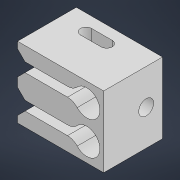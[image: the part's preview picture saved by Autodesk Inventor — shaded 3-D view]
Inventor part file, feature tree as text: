
AUTODESK INVENTOR PART (.ipt)
format: ipt  version: 2022 (Build 260153000, 153)  size: 280,064 bytes
history: native  units: in
note: dims shown in document units (in); Inventor stores cm internally (conversion verified against a paired STEP export)
features: sketch x14, extrude x8, plane x3, projected_geometry x3, chamfer x2, mirror x1
ambient origin geometry x8: Origin, YZ Plane, XZ Plane, XY Plane, X Axis, Y Axis, Z Axis, Center Point
bodies: Solid5 (feature_tree)
feature tree (31):
  plane  "Work Plane1"
  plane  "Work Plane2"
  sketch  "Sketch12"  dims[d45=0.3937in d46=0.0in d47=0.3937in d48=0.0in]
  extrude  "Extrusion15"  Depth=0.6693in TaperAngle=0.0deg
  extrude  "Extrusion16"  Depth=0.0984in TaperAngle=0.0deg
  chamfer  "Chamfer1"  Distance=0.2756in
  chamfer  "Chamfer2"  Distance=0.3937in
  extrude  "Extrusion18"  Depth=0.0787in
  plane  "Work Plane3"
  extrude  "Extrusion19"  Depth=0.1378in
  mirror  "Mirror1"
  extrude  "Extrusion20"  Depth=0.9055in
  extrude  "Extrusion22"  Depth=0.3937in TaperAngle=0.0deg
  extrude  "Extrusion23"  Depth=0.0787in
  extrude  "Extrusion24"  Depth=0.0787in TaperAngle=0.0deg
  sketch  "Sketch1"  dims[d0=1.2997in d1=0.6693in d2=0.0in]
  sketch  "Sketch2"  dims[d3=0.2756in d4=0.0in d5=0.0984in d6=0.0in d7=0.2756in d8=-0.0in]
  sketch  "Sketch3"  dims[d9=0.7579in d12=0.3937in d13=0.0in]
  sketch  "Sketch4"  dims[d14=0.0984in d15=0.2362in d16=0.1575in d17=0.0787in d18=90.0deg d19=0.315in d20=0.8108in]
  sketch  "Sketch6"  dims[d28=0.1181in d29=0.2362in d30=0.1575in d31=0.0787in d32=90.0deg d33=0.315in d34=0.8108in d35=0.0984in]
  sketch  "Sketch7"  dims[d36=0.0984in d37=0.1378in]
  sketch  "Sketch9"  dims[d38=0.1378in d44=0.9055in]
  sketch  "Sketch14"  dims[d49=0.0787in d50=0.0787in d51=45.0deg d52=0.0984in]
  projected_geometry  "Projected Loop2"
  sketch  "Sketch15"  dims[d53=0.0787in d54=0.0787in d55=45.0deg d58=0.0546in d59=0.0in]
  sketch  "Sketch16"  dims[d66=0.1181in]
  projected_geometry  "Projected Loop3"
  sketch  "Sketch18"  dims[d67=0.0787in]
  sketch  "Sketch19"  dims[d68=-0.126in]
  projected_geometry  "Projected Loop4"
  sketch  "Sketch20"  dims[d69=0.3937in d70=0.0in d71=0.126in d72=0.5906in d73=0.0in d78=0.1575in d79=0.2244in d80=0.0in d81=0.1181in d82=0.2505in d83=0.0in d85=0.2505in d86=0.0in d84=0.0059in d87=32.2835in d88=0.0295in d89=46.4567in d90=0.0025in d91=0.0295in d92=0.0148in]
